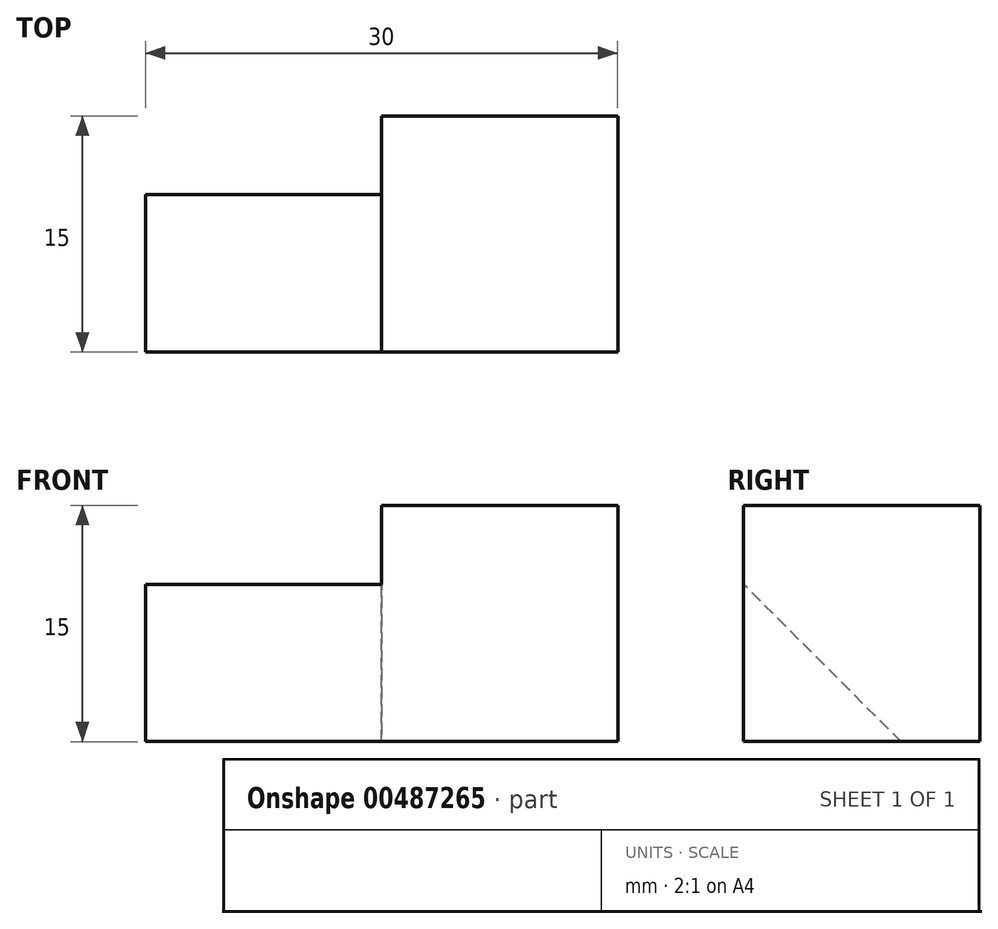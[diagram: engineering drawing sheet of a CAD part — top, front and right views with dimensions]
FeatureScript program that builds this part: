
annotation { "Feature Type Name" : "Feature", "Feature Type Description" : "" }
export const myFeature = defineFeature(function(context is Context, id is Id, definition is map)
    precondition{}
    {
        {
            var Q0;
            Q0=qCreatedBy(makeId("Front.planeOp"),FACE);
            var sketch = newSketch(context, id + "F0", { "sketchPlane" : qUnion([Q0])});
            skLineSegment(sketch, "E0.bottom", {"start": v(8.8, -2.9) * mm, "end": v(23.8, -2.9) * mm});
            skLineSegment(sketch, "E0.top", {"start": v(8.8, -17.9) * mm, "end": v(23.8, -17.9) * mm});
            skLineSegment(sketch, "E0.left", {"start": v(8.8, -2.9) * mm, "end": v(8.8, -17.9) * mm});
            skLineSegment(sketch, "E0.right", {"start": v(23.8, -2.9) * mm, "end": v(23.8, -17.9) * mm});
            skSolve(sketch);
        }
        {
            var Q0;
            Q0=makeQuery(id+"F0.imprint","IMPRINT",FACE,{"disambiguationData":[TD([[makeQuery(id+"F0.imprint","IMPRINT",EDGE,{"derivedFrom":sQuery(id+"F0.wireOp",EDGE,"E0.bottom")}),-1.0]])]});
            extrude(context, id + "F1", {"entities" : qUnion([Q0]), "depth" : 15 * mm});
        }
        {
            var Q0;
            Q0=makeQuery(id+"F1.opExtrude","SWEPT_FACE",FACE,{"disambiguationData":[OSD([sQuery(id+"F0.wireOp",EDGE,"E0.left")])]});
            var sketch = newSketch(context, id + "F2", { "sketchPlane" : qUnion([Q0])});
            skLineSegment(sketch, "E1", {"start": v(5, -17.9) * mm, "end": v(15, -7.9) * mm});
            skLineSegment(sketch, "E2", {"start": v(15, -7.9) * mm, "end": v(15, -17.9) * mm});
            skLineSegment(sketch, "E3", {"start": v(15, -17.9) * mm, "end": v(5, -17.9) * mm});
            skSolve(sketch);
        }
        {
            var Q0;
            Q0=makeQuery(id+"F2.imprint","IMPRINT",FACE,{"disambiguationData":[TD([[makeQuery(id+"F2.imprint","IMPRINT",EDGE,{"derivedFrom":sQuery(id+"F2.wireOp",EDGE,"E1")}),-1.0]])]});
            extrude(context, id + "F3", {"entities" : qUnion([Q0]), "operationType" : NewBodyOperationType.ADD, "depth" : 15 * mm});
        }
    });
